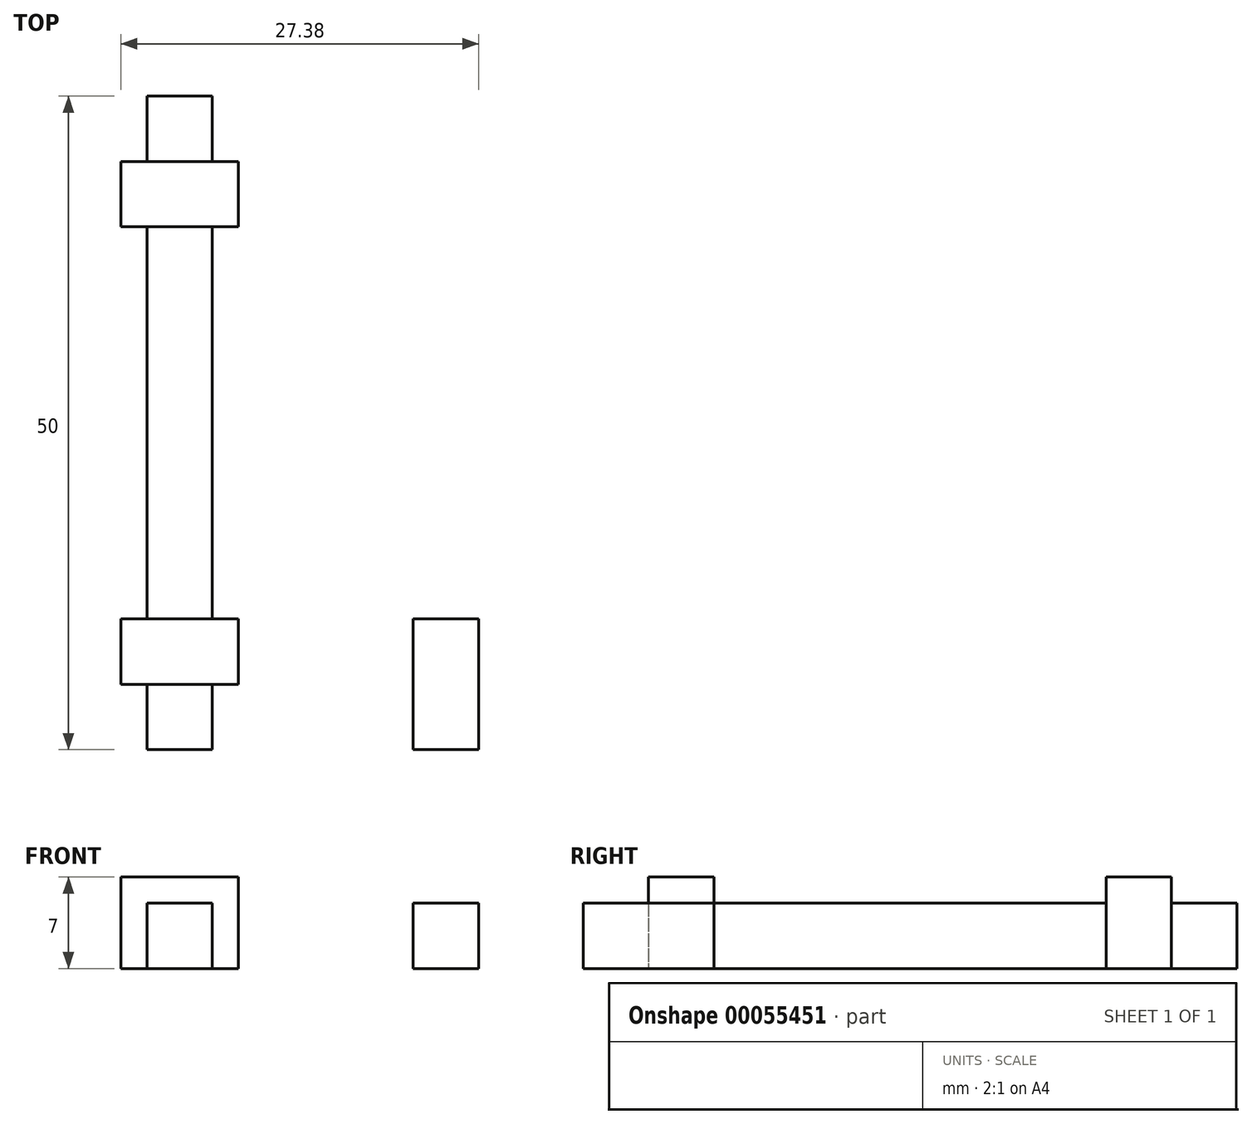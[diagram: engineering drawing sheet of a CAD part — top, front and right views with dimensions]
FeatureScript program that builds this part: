
annotation { "Feature Type Name" : "Feature", "Feature Type Description" : "" }
export const myFeature = defineFeature(function(context is Context, id is Id, definition is map)
    precondition{}
    {
        {
            var Q0;
            Q0=qCreatedBy(makeId("Front.planeOp"),FACE);
            var sketch = newSketch(context, id + "F0", { "sketchPlane" : qUnion([Q0])});
            skLineSegment(sketch, "E0.bottom", {"start": v(-4.07, 7) * mm, "end": v(4.93, 7) * mm});
            skLineSegment(sketch, "E0.top", {"start": v(-4.07, 0) * mm, "end": v(4.93, 0) * mm});
            skLineSegment(sketch, "E0.left", {"start": v(-4.07, 7) * mm, "end": v(-4.07, 0) * mm});
            skLineSegment(sketch, "E0.right", {"start": v(4.93, 7) * mm, "end": v(4.93, 0) * mm});
            skSolve(sketch);
        }
        {
            var Q0;
            Q0=makeQuery(id+"F0.imprint","IMPRINT",FACE,{"disambiguationData":[TD([[makeQuery(id+"F0.imprint","IMPRINT",EDGE,{"derivedFrom":sQuery(id+"F0.wireOp",EDGE,"E0.bottom")}),-1.0]])]});
            extrude(context, id + "F1", {"entities" : qUnion([Q0]), "depth" : 5 * mm});
        }
        {
            var Q0;
            Q0=makeQuery(id+"F1.opExtrude","CAP_FACE",FACE,{"disambiguationData":[OSD([sQuery(id+"F0.wireOp",EDGE,"E0.bottom"),sQuery(id+"F0.wireOp",EDGE,"E0.top"),sQuery(id+"F0.wireOp",EDGE,"E0.left"),sQuery(id+"F0.wireOp",EDGE,"E0.right")])],"isStart":false});
            var sketch = newSketch(context, id + "F2", { "sketchPlane" : qUnion([Q0])});
            skLineSegment(sketch, "E1.bottom", {"start": v(-2.07, 5) * mm, "end": v(2.93, 5) * mm});
            skLineSegment(sketch, "E1.top", {"start": v(-2.07, 0) * mm, "end": v(2.93, 0) * mm});
            skLineSegment(sketch, "E1.left", {"start": v(-2.07, 5) * mm, "end": v(-2.07, 0) * mm});
            skLineSegment(sketch, "E1.right", {"start": v(2.93, 5) * mm, "end": v(2.93, 0) * mm});
            skSolve(sketch);
        }
        {
            var Q0;
            Q0=makeQuery(id+"F2.imprint","IMPRINT",FACE,{"disambiguationData":[TD([[makeQuery(id+"F2.imprint","IMPRINT",EDGE,{"derivedFrom":sQuery(id+"F2.wireOp",EDGE,"E1.bottom")}),-1.0]])]});
            extrude(context, id + "F3", {"entities" : qUnion([Q0]), "operationType" : NewBodyOperationType.ADD, "depth" : 5 * mm});
        }
        {
            var Q0;
            Q0=makeQuery(id+"F0.imprint","IMPRINT",FACE,{"disambiguationData":[TD([[makeQuery(id+"F0.imprint","IMPRINT",EDGE,{"derivedFrom":sQuery(id+"F0.wireOp",EDGE,"E0.bottom")}),-1.0]])]});
            var sketch = newSketch(context, id + "F4", { "sketchPlane" : qUnion([Q0])});
            skLineSegment(sketch, "E2.bottom", {"start": v(2.93, 0) * mm, "end": v(-2.07, 0) * mm});
            skLineSegment(sketch, "E2.top", {"start": v(2.93, 5) * mm, "end": v(-2.07, 5) * mm});
            skLineSegment(sketch, "E2.left", {"start": v(2.93, 0) * mm, "end": v(2.93, 5) * mm});
            skLineSegment(sketch, "E2.right", {"start": v(-2.07, 0) * mm, "end": v(-2.07, 5) * mm});
            skSolve(sketch);
        }
        {
            var Q0;
            Q0=makeQuery(id+"F4.imprint","IMPRINT",FACE,{"disambiguationData":[TD([[makeQuery(id+"F4.imprint","IMPRINT",EDGE,{"derivedFrom":sQuery(id+"F4.wireOp",EDGE,"E2.bottom")}),1.0]])]});
            extrude(context, id + "F5", {"entities" : qUnion([Q0]), "operationType" : NewBodyOperationType.ADD, "oppositeDirection" : true, "depth" : 30 * mm});
        }
        {
            var Q0;
            Q0=makeQuery(id+"F5.opExtrude","CAP_FACE",FACE,{"disambiguationData":[OSD([sQuery(id+"F4.wireOp",EDGE,"E2.bottom"),sQuery(id+"F4.wireOp",EDGE,"E2.top"),sQuery(id+"F4.wireOp",EDGE,"E2.left"),sQuery(id+"F4.wireOp",EDGE,"E2.right")])],"isStart":false});
            var sketch = newSketch(context, id + "F6", { "sketchPlane" : qUnion([Q0])});
            skLineSegment(sketch, "E3.bottom", {"start": v(-4.93, 0) * mm, "end": v(4.07, 0) * mm});
            skLineSegment(sketch, "E3.top", {"start": v(-4.93, 7) * mm, "end": v(4.07, 7) * mm});
            skLineSegment(sketch, "E3.left", {"start": v(-4.93, 0) * mm, "end": v(-4.93, 7) * mm});
            skLineSegment(sketch, "E3.right", {"start": v(4.07, 0) * mm, "end": v(4.07, 7) * mm});
            skSolve(sketch);
        }
        {
            var Q0;
            Q0=makeQuery(id+"F6.imprint","IMPRINT",FACE,{"disambiguationData":[TD([[makeQuery(id+"F6.imprint","IMPRINT",EDGE,{"derivedFrom":sQuery(id+"F6.wireOp",EDGE,"E3.top")}),-1.0]])]});
            var Q1;
            Q1=makeQuery(id+"F6.imprint","IMPRINT",FACE,{"disambiguationData":[TD([[makeQuery(id+"F6.imprint","IMPRINT",EDGE,{"derivedFrom":makeQuery(id+"F5.opExtrude","CAP_EDGE",EDGE,{"disambiguationData":[OSD([sQuery(id+"F4.wireOp",EDGE,"E2.top")])],"isStart":false})}),-1.0]])]});
            extrude(context, id + "F7", {"entities" : qUnion([Q0, Q1]), "operationType" : NewBodyOperationType.ADD, "depth" : 5 * mm});
        }
        {
            var Q0;
            Q0=makeQuery(id+"F7.opExtrude","CAP_FACE",FACE,{"disambiguationData":[OSD([sQuery(id+"F6.wireOp",EDGE,"E3.bottom"),sQuery(id+"F6.wireOp",EDGE,"E3.top"),sQuery(id+"F6.wireOp",EDGE,"E3.left"),sQuery(id+"F6.wireOp",EDGE,"E3.right")])],"isStart":false});
            var sketch = newSketch(context, id + "F8", { "sketchPlane" : qUnion([Q0])});
            skLineSegment(sketch, "E4.bottom", {"start": v(-2.93, 0) * mm, "end": v(2.07, 0) * mm});
            skLineSegment(sketch, "E4.top", {"start": v(-2.93, 5) * mm, "end": v(2.07, 5) * mm});
            skLineSegment(sketch, "E4.left", {"start": v(-2.93, 0) * mm, "end": v(-2.93, 5) * mm});
            skLineSegment(sketch, "E4.right", {"start": v(2.07, 0) * mm, "end": v(2.07, 5) * mm});
            skSolve(sketch);
        }
        {
            var Q0;
            Q0=makeQuery(id+"F8.imprint","IMPRINT",FACE,{"disambiguationData":[TD([[makeQuery(id+"F8.imprint","IMPRINT",EDGE,{"derivedFrom":sQuery(id+"F8.wireOp",EDGE,"E4.bottom")}),1.0]])]});
            extrude(context, id + "F9", {"entities" : qUnion([Q0]), "operationType" : NewBodyOperationType.ADD, "depth" : 5 * mm});
        }
        {
            var Q0;
            Q0=qCreatedBy(makeId("Front.planeOp"),FACE);
            var sketch = newSketch(context, id + "F10", { "sketchPlane" : qUnion([Q0])});
            skLineSegment(sketch, "E5.bottom", {"start": v(18.3, 0) * mm, "end": v(23.3, 0) * mm});
            skLineSegment(sketch, "E5.top", {"start": v(18.3, 5) * mm, "end": v(23.3, 5) * mm});
            skLineSegment(sketch, "E5.left", {"start": v(18.3, 0) * mm, "end": v(18.3, 5) * mm});
            skLineSegment(sketch, "E5.right", {"start": v(23.3, 0) * mm, "end": v(23.3, 5) * mm});
            skSolve(sketch);
        }
        {
            var Q0;
            Q0=makeQuery(id+"F10.imprint","IMPRINT",FACE,{"disambiguationData":[TD([[makeQuery(id+"F10.imprint","IMPRINT",EDGE,{"derivedFrom":sQuery(id+"F10.wireOp",EDGE,"E5.bottom")}),1.0]])]});
            extrude(context, id + "F11", {"entities" : qUnion([Q0]), "depth" : 10 * mm});
        }
    });
